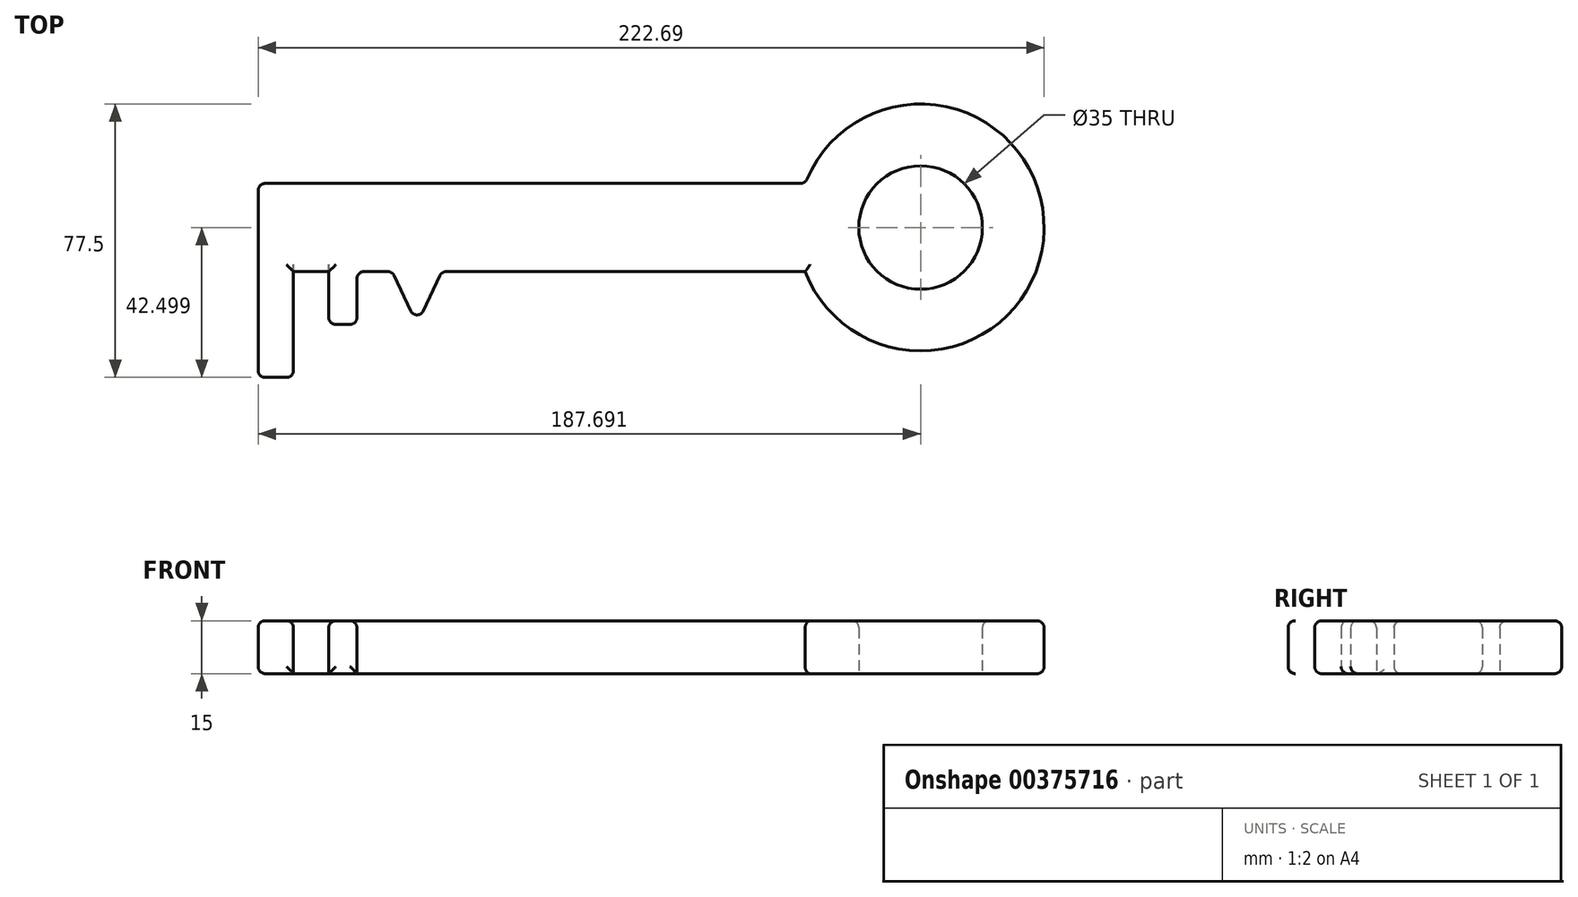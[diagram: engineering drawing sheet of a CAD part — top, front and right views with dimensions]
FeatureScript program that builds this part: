
annotation { "Feature Type Name" : "Feature", "Feature Type Description" : "" }
export const myFeature = defineFeature(function(context is Context, id is Id, definition is map)
    precondition{}
    {
        {
            var Q0;
            Q0=qCreatedBy(makeId("Top.planeOp"),FACE);
            var sketch = newSketch(context, id + "F0", { "sketchPlane" : qUnion([Q0])});
            skLineSegment(sketch, "E0.bottom", {"start": v(-90.12, 52.4) * mm, "end": v(64.88, 52.4) * mm});
            skLineSegment(sketch, "E0.top", {"start": v(-90.12, 27.4) * mm, "end": v(64.88, 27.4) * mm});
            skLineSegment(sketch, "E0.left", {"start": v(-90.12, 52.4) * mm, "end": v(-90.12, 27.4) * mm});
            skLineSegment(sketch, "E0.right", {"start": v(64.88, 52.4) * mm, "end": v(64.88, 27.4) * mm});
            skLineSegment(sketch, "E1.bottom", {"start": v(-90.12, 27.4) * mm, "end": v(-80.12, 27.4) * mm});
            skLineSegment(sketch, "E1.top", {"start": v(-90.12, -2.6) * mm, "end": v(-80.12, -2.6) * mm});
            skLineSegment(sketch, "E1.left", {"start": v(-90.12, 27.4) * mm, "end": v(-90.12, -2.6) * mm});
            skLineSegment(sketch, "E1.right", {"start": v(-80.12, 27.4) * mm, "end": v(-80.12, -2.6) * mm});
            skLineSegment(sketch, "E2.bottom", {"start": v(-70.12, 27.4) * mm, "end": v(-62.12, 27.4) * mm});
            skLineSegment(sketch, "E2.top", {"start": v(-70.12, 12.4) * mm, "end": v(-62.12, 12.4) * mm});
            skLineSegment(sketch, "E2.left", {"start": v(-70.12, 27.4) * mm, "end": v(-70.12, 12.4) * mm});
            skLineSegment(sketch, "E2.right", {"start": v(-62.12, 27.4) * mm, "end": v(-62.12, 12.4) * mm});
            skLineSegment(sketch, "E3", {"start": v(-52.12, 27.4) * mm, "end": v(-45.12, 12.4) * mm});
            skLineSegment(sketch, "E4", {"start": v(-45.12, 12.4) * mm, "end": v(-38.12, 27.4) * mm});
            skLineSegment(sketch, "E5.bottom", {"start": v(-52.12, 27.4) * mm, "end": v(-45.12, 27.4) * mm});
            skArc(sketch, "E6", {"start": v(64.88, 27.4) * mm, "mid": v(132.57, 39.9) * mm, "end": v(64.88, 52.4) * mm});
            skCircle(sketch, "E7", {"center": v(97.57, 39.9) * mm, "radius": 17.5 * mm});
            skSolve(sketch);
        }
        {
            var Q0;
            Q0 = qSketchRegion(id + "F0", true);
            extrude(context, id + "F1", {"entities" : qUnion([Q0]), "depth" : 15 * mm});
        }
        {
            var Q0;
            {var subQ0=sQuery(id+"F0.wireOp",EDGE,"E0.top");Q0=makeQuery(id+"F1.opExtrude","CAP_EDGE",EDGE,{"disambiguationData":[OSD([subQ0]),TDD([makeQuery(id+"F0.imprint","IMPRINT",EDGE,{"disambiguationData":[TD([[makeQuery(id+"F0.imprint","INTERSECT",VERTEX,{"derivedFrom":[subQ0,sQuery(id+"F0.wireOp",EDGE,"E1.bottom"),sQuery(id+"F0.wireOp",EDGE,"E1.right")]}),-1.0]])],"derivedFrom":subQ0})])],"isStart":false});}
            var Q1;
            Q1=makeQuery(id+"F1.opExtrude","CAP_EDGE",EDGE,{"disambiguationData":[OSD([sQuery(id+"F0.wireOp",EDGE,"E2.left")])],"isStart":false});
            var Q2;
            Q2=makeQuery(id+"F1.opExtrude","CAP_EDGE",EDGE,{"disambiguationData":[OSD([sQuery(id+"F0.wireOp",EDGE,"E2.right")])],"isStart":false});
            var Q3;
            Q3=makeQuery(id+"F1.opExtrude","CAP_EDGE",EDGE,{"disambiguationData":[OSD([sQuery(id+"F0.wireOp",EDGE,"E2.top")])],"isStart":true});
            var Q4;
            Q4=makeQuery(id+"F1.opExtrude","SWEPT_EDGE",EDGE,{"disambiguationData":[OSD([sQuery(id+"F0.wireOp",EDGE,"E2.top"),sQuery(id+"F0.wireOp",EDGE,"E2.right")])]});
            var Q5;
            Q5=makeQuery(id+"F1.opExtrude","SWEPT_EDGE",EDGE,{"disambiguationData":[OSD([sQuery(id+"F0.wireOp",EDGE,"E2.top"),sQuery(id+"F0.wireOp",EDGE,"E2.left")])]});
            var Q6;
            Q6=makeQuery(id+"F1.opExtrude","CAP_EDGE",EDGE,{"disambiguationData":[OSD([sQuery(id+"F0.wireOp",EDGE,"E1.right")])],"isStart":false});
            var Q7;
            Q7=makeQuery(id+"F1.opExtrude","CAP_EDGE",EDGE,{"disambiguationData":[OSD([sQuery(id+"F0.wireOp",EDGE,"E1.top")])],"isStart":false});
            var Q8;
            Q8=makeQuery(id+"F1.opExtrude","CAP_EDGE",EDGE,{"disambiguationData":[OSD([sQuery(id+"F0.wireOp",EDGE,"E1.top")])],"isStart":true});
            var Q9;
            Q9=makeQuery(id+"F1.opExtrude","SWEPT_EDGE",EDGE,{"disambiguationData":[OSD([sQuery(id+"F0.wireOp",EDGE,"E1.top"),sQuery(id+"F0.wireOp",EDGE,"E1.left")])]});
            var Q10;
            Q10=makeQuery(id+"F1.opExtrude","SWEPT_EDGE",EDGE,{"disambiguationData":[OSD([sQuery(id+"F0.wireOp",EDGE,"E1.top"),sQuery(id+"F0.wireOp",EDGE,"E1.right")])]});
            var Q11;
            {var subQ0=sQuery(id+"F0.wireOp",EDGE,"E0.top");Q11=makeQuery(id+"F1.opExtrude","CAP_EDGE",EDGE,{"disambiguationData":[OSD([subQ0]),TDD([makeQuery(id+"F0.imprint","IMPRINT",EDGE,{"disambiguationData":[TD([[makeQuery(id+"F0.imprint","INTERSECT",VERTEX,{"derivedFrom":[subQ0,sQuery(id+"F0.wireOp",EDGE,"E1.bottom"),sQuery(id+"F0.wireOp",EDGE,"E1.right")]}),-1.0]])],"derivedFrom":subQ0})])],"isStart":true});}
            var Q12;
            Q12=makeQuery(id+"F1.opExtrude","CAP_EDGE",EDGE,{"disambiguationData":[OSD([sQuery(id+"F0.wireOp",EDGE,"E2.top")])],"isStart":false});
            var Q13;
            {var subQ0=sQuery(id+"F0.wireOp",EDGE,"E0.top");Q13=makeQuery(id+"F1.opExtrude","SWEPT_FACE",FACE,{"disambiguationData":[OSD([subQ0]),TDD([makeQuery(id+"F0.imprint","IMPRINT",EDGE,{"disambiguationData":[TD([[makeQuery(id+"F0.imprint","INTERSECT",VERTEX,{"derivedFrom":[subQ0,sQuery(id+"F0.wireOp",EDGE,"E2.bottom"),sQuery(id+"F0.wireOp",EDGE,"E2.right")]}),-1.0]])],"derivedFrom":subQ0})])]});}
            var Q14;
            Q14=makeQuery(id+"F1.opExtrude","CAP_FACE",FACE,{"disambiguationData":[OSD([sQuery(id+"F0.wireOp",EDGE,"E0.bottom"),sQuery(id+"F0.wireOp",EDGE,"E0.top"),sQuery(id+"F0.wireOp",EDGE,"E0.left"),sQuery(id+"F0.wireOp",EDGE,"E1.top"),sQuery(id+"F0.wireOp",EDGE,"E1.left"),sQuery(id+"F0.wireOp",EDGE,"E1.right"),sQuery(id+"F0.wireOp",EDGE,"E2.top"),sQuery(id+"F0.wireOp",EDGE,"E2.left"),sQuery(id+"F0.wireOp",EDGE,"E2.right"),sQuery(id+"F0.wireOp",EDGE,"E3"),sQuery(id+"F0.wireOp",EDGE,"E4"),sQuery(id+"F0.wireOp",EDGE,"E6"),sQuery(id+"F0.wireOp",EDGE,"E7")])],"isStart":false});
            var Q15;
            Q15=makeQuery(id+"F1.opExtrude","SWEPT_FACE",FACE,{"disambiguationData":[OSD([sQuery(id+"F0.wireOp",EDGE,"E4")])]});
            var Q16;
            Q16=makeQuery(id+"F1.opExtrude","CAP_EDGE",EDGE,{"disambiguationData":[OSD([sQuery(id+"F0.wireOp",EDGE,"E3")])],"isStart":true});
            var Q17;
            {var subQ0=sQuery(id+"F0.wireOp",EDGE,"E0.top");Q17=makeQuery(id+"F1.opExtrude","CAP_EDGE",EDGE,{"disambiguationData":[OSD([subQ0]),TDD([makeQuery(id+"F0.imprint","IMPRINT",EDGE,{"disambiguationData":[TD([[makeQuery(id+"F0.imprint","INTERSECT",VERTEX,{"derivedFrom":[subQ0,sQuery(id+"F0.wireOp",EDGE,"E4")]}),-1.0]])],"derivedFrom":subQ0})])],"isStart":true});}
            var Q18;
            Q18=makeQuery(id+"F1.opExtrude","CAP_EDGE",EDGE,{"disambiguationData":[OSD([sQuery(id+"F0.wireOp",EDGE,"E6")])],"isStart":true});
            var Q19;
            Q19=makeQuery(id+"F1.opExtrude","CAP_EDGE",EDGE,{"disambiguationData":[OSD([sQuery(id+"F0.wireOp",EDGE,"E7")])],"isStart":false});
            var Q20;
            Q20=makeQuery(id+"F1.opExtrude","CAP_EDGE",EDGE,{"disambiguationData":[OSD([sQuery(id+"F0.wireOp",EDGE,"E0.left"),sQuery(id+"F0.wireOp",EDGE,"E1.left")])],"isStart":false});
            var Q21;
            Q21=makeQuery(id+"F1.opExtrude","CAP_EDGE",EDGE,{"disambiguationData":[OSD([sQuery(id+"F0.wireOp",EDGE,"E0.bottom")])],"isStart":true});
            var Q22;
            Q22=makeQuery(id+"F1.opExtrude","SWEPT_FACE",FACE,{"disambiguationData":[OSD([sQuery(id+"F0.wireOp",EDGE,"E0.bottom")])]});
            var Q23;
            Q23=makeQuery(id+"F1.opExtrude","CAP_EDGE",EDGE,{"disambiguationData":[OSD([sQuery(id+"F0.wireOp",EDGE,"E0.left"),sQuery(id+"F0.wireOp",EDGE,"E1.left")])],"isStart":true});
            fillet(context, id + "F2", {"entities" : qUnion([Q0, Q1, Q2, Q3, Q4, Q5, Q6, Q7, Q8, Q9, Q10, Q11, Q12, Q13, Q14, Q15, Q16, Q17, Q18, Q19, Q20, Q21, Q22, Q23]), "radius" : 2 * mm, "tangentPropagation" : true, "allowEdgeOverflow" : false});
        }
    });
